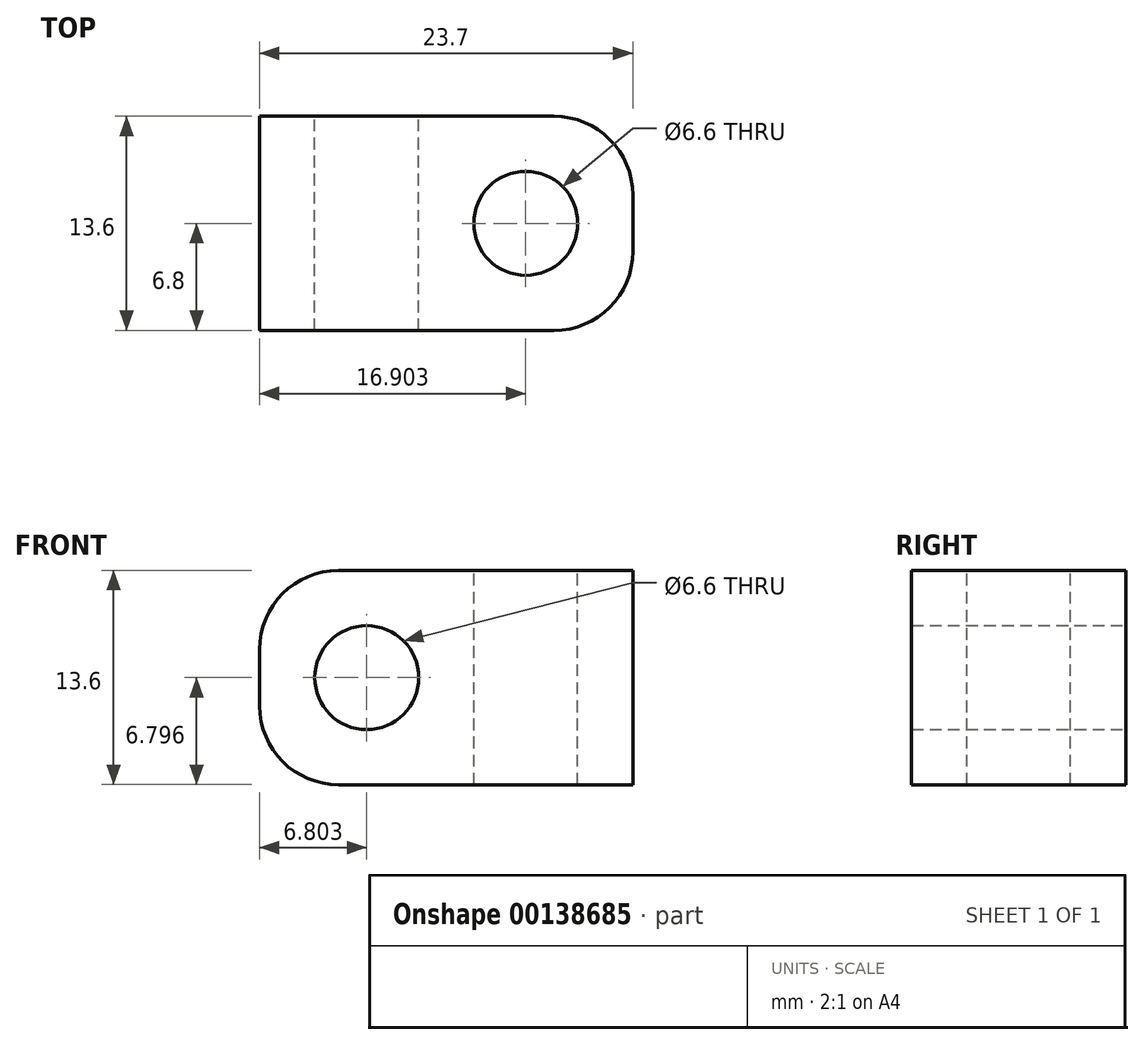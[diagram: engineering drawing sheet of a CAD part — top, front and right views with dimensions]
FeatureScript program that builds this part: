
annotation { "Feature Type Name" : "Feature", "Feature Type Description" : "" }
export const myFeature = defineFeature(function(context is Context, id is Id, definition is map)
    precondition{}
    {
        {
            var Q0;
            Q0=qCreatedBy(makeId("Front.planeOp"),FACE);
            var sketch = newSketch(context, id + "F0", { "sketchPlane" : qUnion([Q0])});
            skLineSegment(sketch, "E0.bottom", {"start": v(-21.87, 30.84) * mm, "end": v(1.83, 30.84) * mm});
            skLineSegment(sketch, "E0.top", {"start": v(-21.87, 17.24) * mm, "end": v(1.83, 17.24) * mm});
            skLineSegment(sketch, "E0.left", {"start": v(-21.87, 30.84) * mm, "end": v(-21.87, 17.24) * mm});
            skLineSegment(sketch, "E0.right", {"start": v(1.83, 30.84) * mm, "end": v(1.83, 17.24) * mm});
            skLineSegment(sketch, "E1", {"start": v(-21.87, 24.04) * mm, "end": v(-8.27, 24.04) * mm, "construction": true});
            skCircle(sketch, "E2", {"center": v(-15.07, 24.04) * mm, "radius": 3.3 * mm});
            skCircle(sketch, "E3", {"center": v(-4.97, 24.04) * mm, "radius": 3.3 * mm, "construction": true});
            skSolve(sketch);
        }
        {
            var Q0;
            Q0 = qSketchRegion(id + "F0", true);
            extrude(context, id + "F1", {"entities" : qUnion([Q0]), "depth" : 13.6 * mm});
        }
        {
            var Q0;
            Q0=makeQuery(id+"F1.opExtrude","SWEPT_FACE",FACE,{"disambiguationData":[OSD([sQuery(id+"F0.wireOp",EDGE,"E0.bottom")])]});
            var sketch = newSketch(context, id + "F2", { "sketchPlane" : qUnion([Q0])});
            skLineSegment(sketch, "E4", {"start": v(1.83, -6.8) * mm, "end": v(-11.77, -6.8) * mm, "construction": true});
            skCircle(sketch, "E5", {"center": v(-4.97, -6.8) * mm, "radius": 3.3 * mm});
            skLineSegment(sketch, "E6", {"start": v(1.83, -13.6) * mm, "end": v(1.83, 0) * mm});
            skSolve(sketch);
        }
        {
            var Q0;
            Q0 = qSketchRegion(id + "F2", true);
            extrude(context, id + "F3", {"entities" : qUnion([Q0]), "operationType" : NewBodyOperationType.REMOVE, "endBound" : BoundingType.THROUGH_ALL, "oppositeDirection" : true, "depth" : 25 * mm});
        }
        {
            var Q0;
            Q0=makeQuery(id+"F1.opExtrude","CAP_EDGE",EDGE,{"disambiguationData":[OSD([sQuery(id+"F0.wireOp",EDGE,"E0.right")])],"isStart":false});
            var Q1;
            Q1=makeQuery(id+"F1.opExtrude","CAP_EDGE",EDGE,{"disambiguationData":[OSD([sQuery(id+"F0.wireOp",EDGE,"E0.right")])],"isStart":true});
            var Q2;
            Q2=makeQuery(id+"F1.opExtrude","SWEPT_EDGE",EDGE,{"disambiguationData":[OSD([sQuery(id+"F0.wireOp",EDGE,"E0.bottom"),sQuery(id+"F0.wireOp",EDGE,"E0.left")])]});
            var Q3;
            Q3=makeQuery(id+"F1.opExtrude","SWEPT_EDGE",EDGE,{"disambiguationData":[OSD([sQuery(id+"F0.wireOp",EDGE,"E0.top"),sQuery(id+"F0.wireOp",EDGE,"E0.left")])]});
            fillet(context, id + "F4", {"entities" : qUnion([Q0, Q1, Q2, Q3]), "radius" : 5 * mm, "tangentPropagation" : true, "allowEdgeOverflow" : false});
        }
    });
